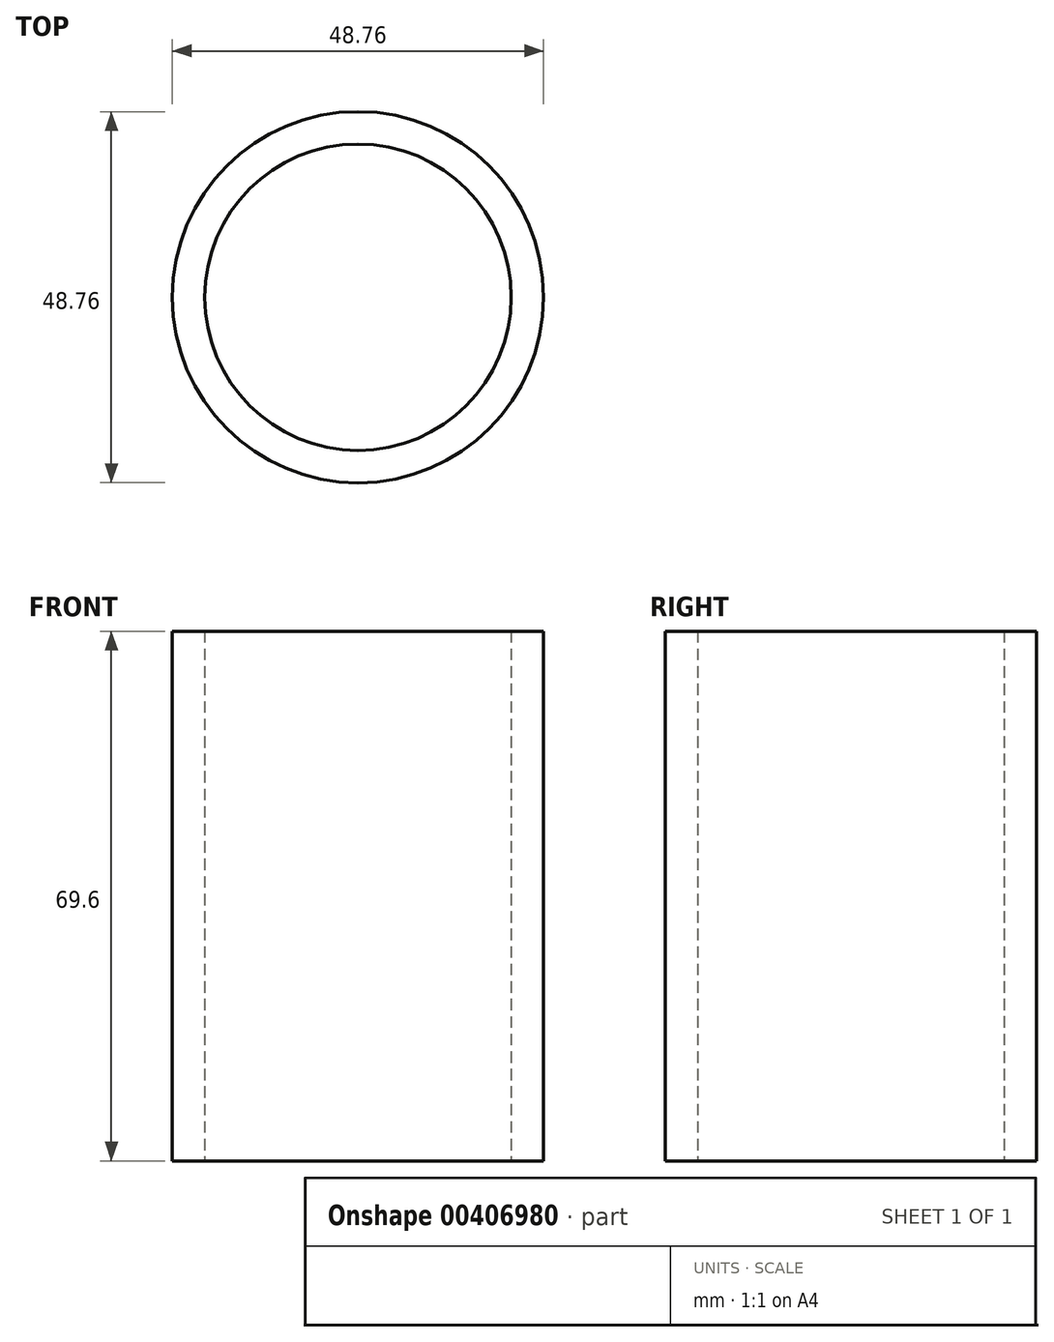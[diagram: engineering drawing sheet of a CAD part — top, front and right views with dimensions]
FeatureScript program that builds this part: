
annotation { "Feature Type Name" : "Feature", "Feature Type Description" : "" }
export const myFeature = defineFeature(function(context is Context, id is Id, definition is map)
    precondition{}
    {
        {
            var Q0;
            Q0=qCreatedBy(makeId("Top.planeOp"),FACE);
            var sketch = newSketch(context, id + "F0", { "sketchPlane" : qUnion([Q0])});
            skCircle(sketch, "E0", {"center": v(0, 0) * mm, "radius": 20.13 * mm});
            skCircle(sketch, "E1", {"center": v(0, 0) * mm, "radius": 24.38 * mm});
            skSolve(sketch);
        }
        {
            var Q0;
            Q0=makeQuery(id+"F0.imprint","IMPRINT",FACE,{"disambiguationData":[TD([[makeQuery(id+"F0.imprint","IMPRINT",EDGE,{"derivedFrom":sQuery(id+"F0.wireOp",EDGE,"E0")}),-1.0]])]});
            extrude(context, id + "F1", {"entities" : qUnion([Q0]), "depth" : 69.6 * mm});
        }
    });
